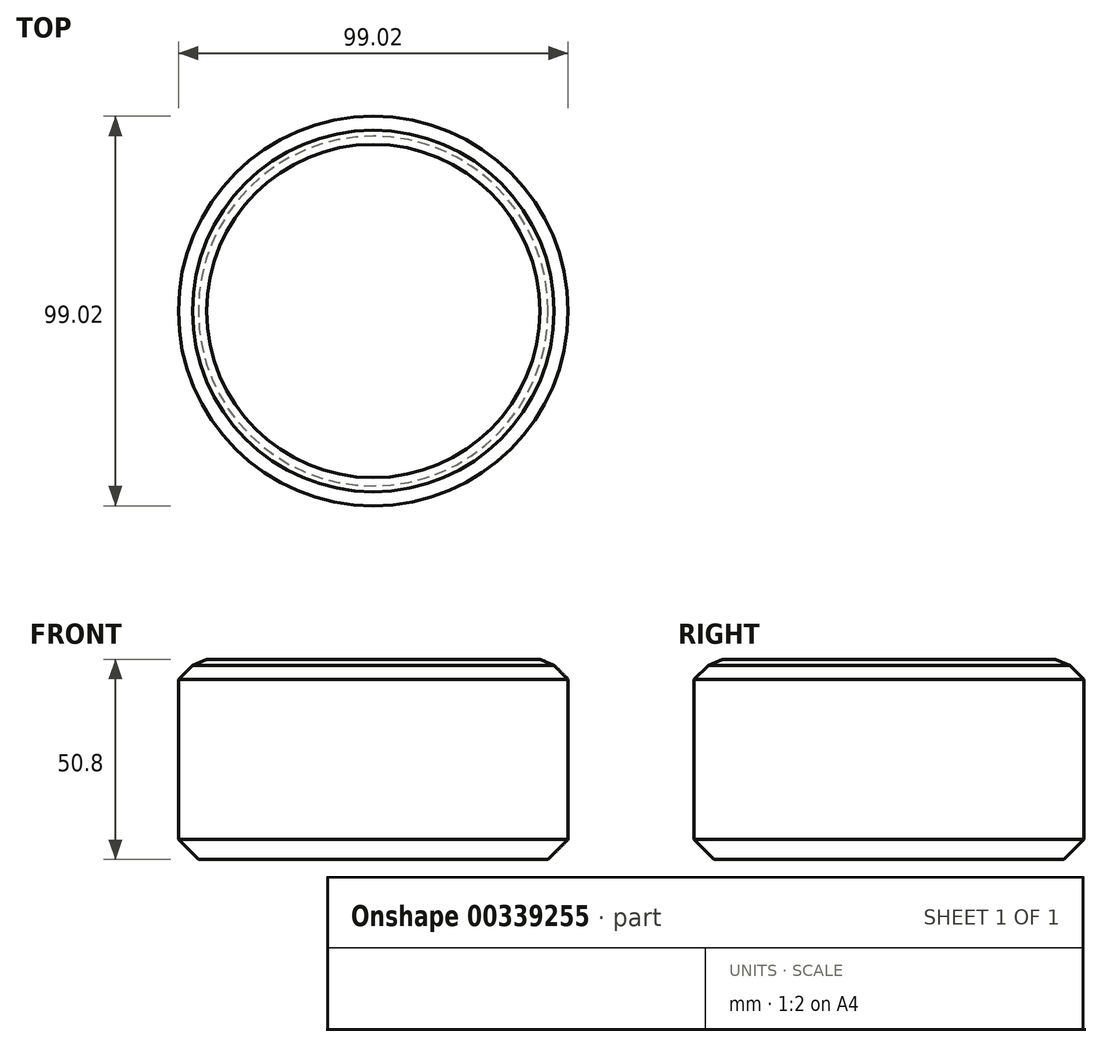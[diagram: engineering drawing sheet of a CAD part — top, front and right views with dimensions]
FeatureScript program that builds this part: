
annotation { "Feature Type Name" : "Feature", "Feature Type Description" : "" }
export const myFeature = defineFeature(function(context is Context, id is Id, definition is map)
    precondition{}
    {
        {
            var Q0;
            Q0=qCreatedBy(makeId("Top.planeOp"),FACE);
            var sketch = newSketch(context, id + "F0", { "sketchPlane" : qUnion([Q0])});
            skCircle(sketch, "E0", {"center": v(0, 0) * mm, "radius": 49.5 * mm});
            skSolve(sketch);
        }
        {
            var Q0;
            Q0=makeQuery(id+"F0.imprint","IMPRINT",FACE,{"disambiguationData":[TD([[makeQuery(id+"F0.imprint","IMPRINT",EDGE,{"derivedFrom":sQuery(id+"F0.wireOp",EDGE,"E0")}),1.0]])]});
            extrude(context, id + "F1", {"entities" : qUnion([Q0]), "depth" : 50.8 * mm});
        }
        {
            var Q0;
            Q0=makeQuery(id+"F1.opExtrude","CAP_EDGE",EDGE,{"disambiguationData":[OSD([sQuery(id+"F0.wireOp",EDGE,"E0")])],"isStart":false});
            var Q1;
            Q1=makeQuery(id+"F1.opExtrude","CAP_EDGE",EDGE,{"disambiguationData":[OSD([sQuery(id+"F0.wireOp",EDGE,"E0")])],"isStart":true});
            chamfer(context, id + "F2", {"entities" : qUnion([Q0, Q1]), "width" : 5.08 * mm, "tangentPropagation" : true});
        }
        {
            var Q0;
            Q0=makeQuery(id+"F1.opExtrude","CAP_FACE",FACE,{"disambiguationData":[OSD([sQuery(id+"F0.wireOp",EDGE,"E0")])],"isStart":false});
            chamfer(context, id + "F3", {"entities" : qUnion([Q0]), "width" : 5.08 * mm, "tangentPropagation" : true});
        }
    });
